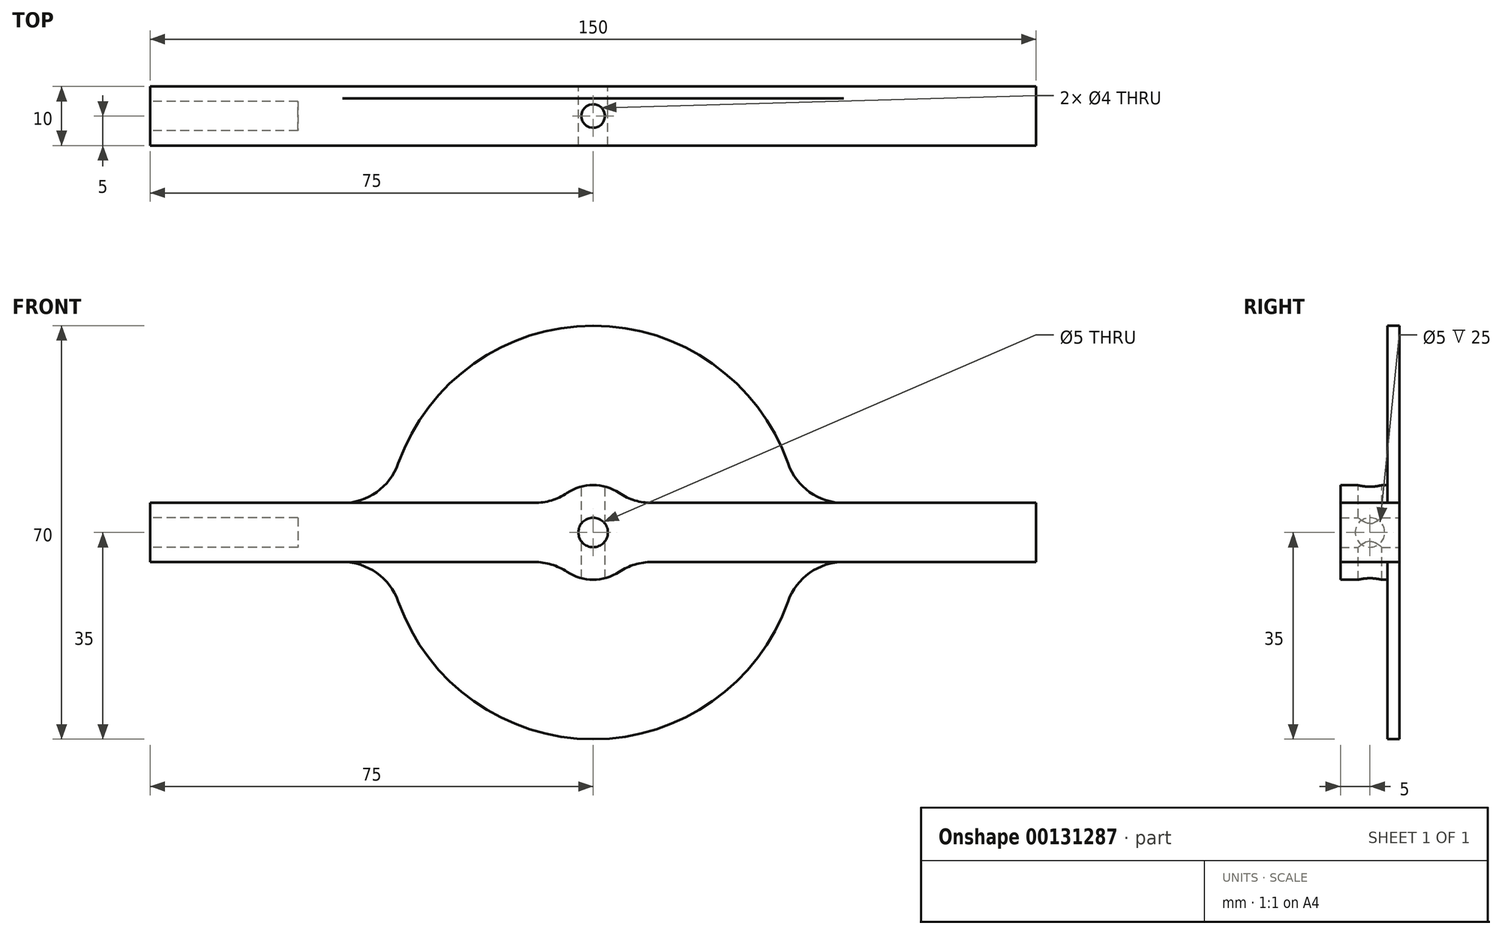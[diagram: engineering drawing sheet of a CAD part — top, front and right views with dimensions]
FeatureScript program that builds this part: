
annotation { "Feature Type Name" : "Feature", "Feature Type Description" : "" }
export const myFeature = defineFeature(function(context is Context, id is Id, definition is map)
    precondition{}
    {
        {
            var Q0;
            Q0=qCreatedBy(makeId("Front.planeOp"),FACE);
            var sketch = newSketch(context, id + "F0", { "sketchPlane" : qUnion([Q0])});
            skCircle(sketch, "E0", {"center": v(0, 0) * mm, "radius": 2.5 * mm});
            skLineSegment(sketch, "E1.bottom", {"start": v(6.24, 5) * mm, "end": v(75, 5) * mm});
            skLineSegment(sketch, "E1.top", {"start": v(6.24, -5) * mm, "end": v(75, -5) * mm});
            skLineSegment(sketch, "E1.left", {"start": v(6.24, 5) * mm, "end": v(6.24, -5) * mm, "construction": true});
            skLineSegment(sketch, "E1.right", {"start": v(75, 5) * mm, "end": v(75, -5) * mm});
            skLineSegment(sketch, "E2.bottom", {"start": v(-6.24, 5) * mm, "end": v(-75, 5) * mm});
            skLineSegment(sketch, "E2.top", {"start": v(-6.24, -5) * mm, "end": v(-75, -5) * mm});
            skLineSegment(sketch, "E2.left", {"start": v(-6.24, 5) * mm, "end": v(-6.24, -5) * mm, "construction": true});
            skLineSegment(sketch, "E2.right", {"start": v(-75, 5) * mm, "end": v(-75, -5) * mm});
            skLineSegment(sketch, "E3", {"start": v(-6.24, 5) * mm, "end": v(6.24, 5) * mm, "construction": true});
            skLineSegment(sketch, "E4", {"start": v(-6.24, -5) * mm, "end": v(6.24, -5) * mm, "construction": true});
            skArc(sketch, "E5", {"start": v(-6.24, 5) * mm, "mid": v(-8, 0) * mm, "end": v(-6.24, -5) * mm, "construction": true});
            skArc(sketch, "E6", {"start": v(-6.24, -5) * mm, "mid": v(0, -8) * mm, "end": v(6.24, -5) * mm});
            skArc(sketch, "E7", {"start": v(6.24, -5) * mm, "mid": v(8, 0) * mm, "end": v(6.24, 5) * mm, "construction": true});
            skArc(sketch, "E8", {"start": v(6.24, 5) * mm, "mid": v(0, 8) * mm, "end": v(-6.24, 5) * mm});
            skSolve(sketch);
        }
        {
            var Q0;
            Q0 = qSketchRegion(id + "F0", true);
            extrude(context, id + "F1", {"entities" : qUnion([Q0]), "depth" : 10 * mm});
        }
        {
            var Q0;
            Q0=makeQuery(id+"F1.opExtrude","CAP_FACE",FACE,{"disambiguationData":[OSD([sQuery(id+"F0.wireOp",EDGE,"E0"),sQuery(id+"F0.wireOp",EDGE,"E1.bottom"),sQuery(id+"F0.wireOp",EDGE,"E1.top"),sQuery(id+"F0.wireOp",EDGE,"E1.right"),sQuery(id+"F0.wireOp",EDGE,"E2.bottom"),sQuery(id+"F0.wireOp",EDGE,"E2.top"),sQuery(id+"F0.wireOp",EDGE,"E2.right"),sQuery(id+"F0.wireOp",EDGE,"E6"),sQuery(id+"F0.wireOp",EDGE,"E8")])],"isStart":true});
            var sketch = newSketch(context, id + "F2", { "sketchPlane" : qUnion([Q0])});
            skCircle(sketch, "E9", {"center": v(0, 0) * mm, "radius": 35 * mm});
            skCircle(sketch, "E10.0", {"center": v(0, 0) * mm, "radius": 2.5 * mm});
            skSolve(sketch);
        }
        {
            var Q0;
            Q0 = qSketchRegion(id + "F2", true);
            extrude(context, id + "F3", {"entities" : qUnion([Q0]), "operationType" : NewBodyOperationType.ADD, "oppositeDirection" : true, "depth" : 2 * mm});
        }
        {
            var Q0;
            Q0=makeQuery(id+"F1.opExtrude","SWEPT_FACE",FACE,{"disambiguationData":[OSD([sQuery(id+"F0.wireOp",EDGE,"E2.right")])]});
            var sketch = newSketch(context, id + "F4", { "sketchPlane" : qUnion([Q0])});
            skCircle(sketch, "E11", {"center": v(5, 0) * mm, "radius": 2.5 * mm});
            skLineSegment(sketch, "E12", {"start": v(0, 5) * mm, "end": v(10, -5) * mm, "construction": true});
            skSolve(sketch);
        }
        {
            var Q0;
            Q0 = qSketchRegion(id + "F4", true);
            extrude(context, id + "F5", {"entities" : qUnion([Q0]), "operationType" : NewBodyOperationType.REMOVE, "oppositeDirection" : true, "depth" : 25 * mm});
        }
        {
            var Q0;
            Q0=qCreatedBy(makeId("Top.planeOp"),FACE);
            var sketch = newSketch(context, id + "F6", { "sketchPlane" : qUnion([Q0])});
            skCircle(sketch, "E13", {"center": v(0, -5) * mm, "radius": 2 * mm});
            skSolve(sketch);
        }
        {
            var Q0;
            Q0 = qSketchRegion(id + "F6", true);
            extrude(context, id + "F7", {"entities" : qUnion([Q0]), "operationType" : NewBodyOperationType.REMOVE, "endBound" : BoundingType.THROUGH_ALL, "oppositeDirection" : true, "depth" : 25 * mm, "hasSecondDirection" : true, "secondDirectionBound" : SecondDirectionBoundingType.THROUGH_ALL, "secondDirectionOppositeDirection" : false, "secondDirectionDepth" : 25 * mm});
        }
        {
            var Q0;
            Q0=makeQuery(id+"F1.opExtrude","SWEPT_EDGE",EDGE,{"disambiguationData":[OSD([sQuery(id+"F0.wireOp",EDGE,"E2.bottom"),sQuery(id+"F0.wireOp",EDGE,"E8")])]});
            var Q1;
            Q1=makeQuery(id+"F1.opExtrude","SWEPT_EDGE",EDGE,{"disambiguationData":[OSD([sQuery(id+"F0.wireOp",EDGE,"E1.bottom"),sQuery(id+"F0.wireOp",EDGE,"E8")])]});
            var Q2;
            Q2=makeQuery(id+"F1.opExtrude","SWEPT_EDGE",EDGE,{"disambiguationData":[OSD([sQuery(id+"F0.wireOp",EDGE,"E1.top"),sQuery(id+"F0.wireOp",EDGE,"E6")])]});
            var Q3;
            Q3=makeQuery(id+"F1.opExtrude","SWEPT_EDGE",EDGE,{"disambiguationData":[OSD([sQuery(id+"F0.wireOp",EDGE,"E2.top"),sQuery(id+"F0.wireOp",EDGE,"E6")])]});
            var Q4;
            Q4=makeQuery(id+"F3.boolean.opBoolean","INTERSECT",EDGE,{"derivedFrom":[makeQuery(id+"F1.opExtrude","SWEPT_FACE",FACE,{"disambiguationData":[OSD([sQuery(id+"F0.wireOp",EDGE,"E1.bottom")])]}),makeQuery(id+"F3.opExtrude","SWEPT_FACE",FACE,{"disambiguationData":[OSD([sQuery(id+"F2.wireOp",EDGE,"E9")])]})]});
            var Q5;
            Q5=makeQuery(id+"F3.boolean.opBoolean","INTERSECT",EDGE,{"derivedFrom":[makeQuery(id+"F1.opExtrude","SWEPT_FACE",FACE,{"disambiguationData":[OSD([sQuery(id+"F0.wireOp",EDGE,"E1.top")])]}),makeQuery(id+"F3.opExtrude","SWEPT_FACE",FACE,{"disambiguationData":[OSD([sQuery(id+"F2.wireOp",EDGE,"E9")])]})]});
            var Q6;
            Q6=makeQuery(id+"F3.boolean.opBoolean","INTERSECT",EDGE,{"derivedFrom":[makeQuery(id+"F1.opExtrude","SWEPT_FACE",FACE,{"disambiguationData":[OSD([sQuery(id+"F0.wireOp",EDGE,"E2.top")])]}),makeQuery(id+"F3.opExtrude","SWEPT_FACE",FACE,{"disambiguationData":[OSD([sQuery(id+"F2.wireOp",EDGE,"E9")])]})]});
            var Q7;
            Q7=makeQuery(id+"F3.boolean.opBoolean","INTERSECT",EDGE,{"derivedFrom":[makeQuery(id+"F1.opExtrude","SWEPT_FACE",FACE,{"disambiguationData":[OSD([sQuery(id+"F0.wireOp",EDGE,"E2.bottom")])]}),makeQuery(id+"F3.opExtrude","SWEPT_FACE",FACE,{"disambiguationData":[OSD([sQuery(id+"F2.wireOp",EDGE,"E9")])]})]});
            fillet(context, id + "F8", {"entities" : qUnion([Q0, Q1, Q2, Q3, Q4, Q5, Q6, Q7]), "radius" : 10 * mm, "tangentPropagation" : true, "allowEdgeOverflow" : false});
        }
    });
